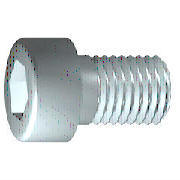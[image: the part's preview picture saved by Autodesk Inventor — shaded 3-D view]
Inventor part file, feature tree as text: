
AUTODESK INVENTOR PART (.ipt)
format: ipt  version: 2019 (Build 230136000, 136)  size: 185,856 bytes
history: native  units: mm (DEFAULTED — no unit token found)
features: sketch x2, extrude x1, plane x1, fillet x1
ambient origin geometry x7: Origin, YZ Plane, XY Plane, X Axis, Y Axis, Z Axis, Center Point
bodies: Solid1 (feature_tree), Body (feature_tree)
feature tree (5):
  extrude  "Slot"  Depth=3.0mm
  plane  "Work Plane1"
  fillet  "Fillet2"  Radius=3.0mm
  sketch  "Sketch1"  dims[d1=18.0mm d2=0.306825mm d3=3.0mm]
  sketch  "Sketch2"  dims[d4=1.3mm d5=60.0deg d6=3.0mm d7=3.0mm d8=2.886751mm d9=5.5mm d10=90.0deg d11=10.0mm d12=0.0mm d13=18.0mm d14=0.0mm d15=0.306725mm d16=0.306725mm d17=0.3mm d19=0.0mm d26=30.0mm d27=45.0deg d28=0.0mm d29=0.0mm d30=0.1mm]
